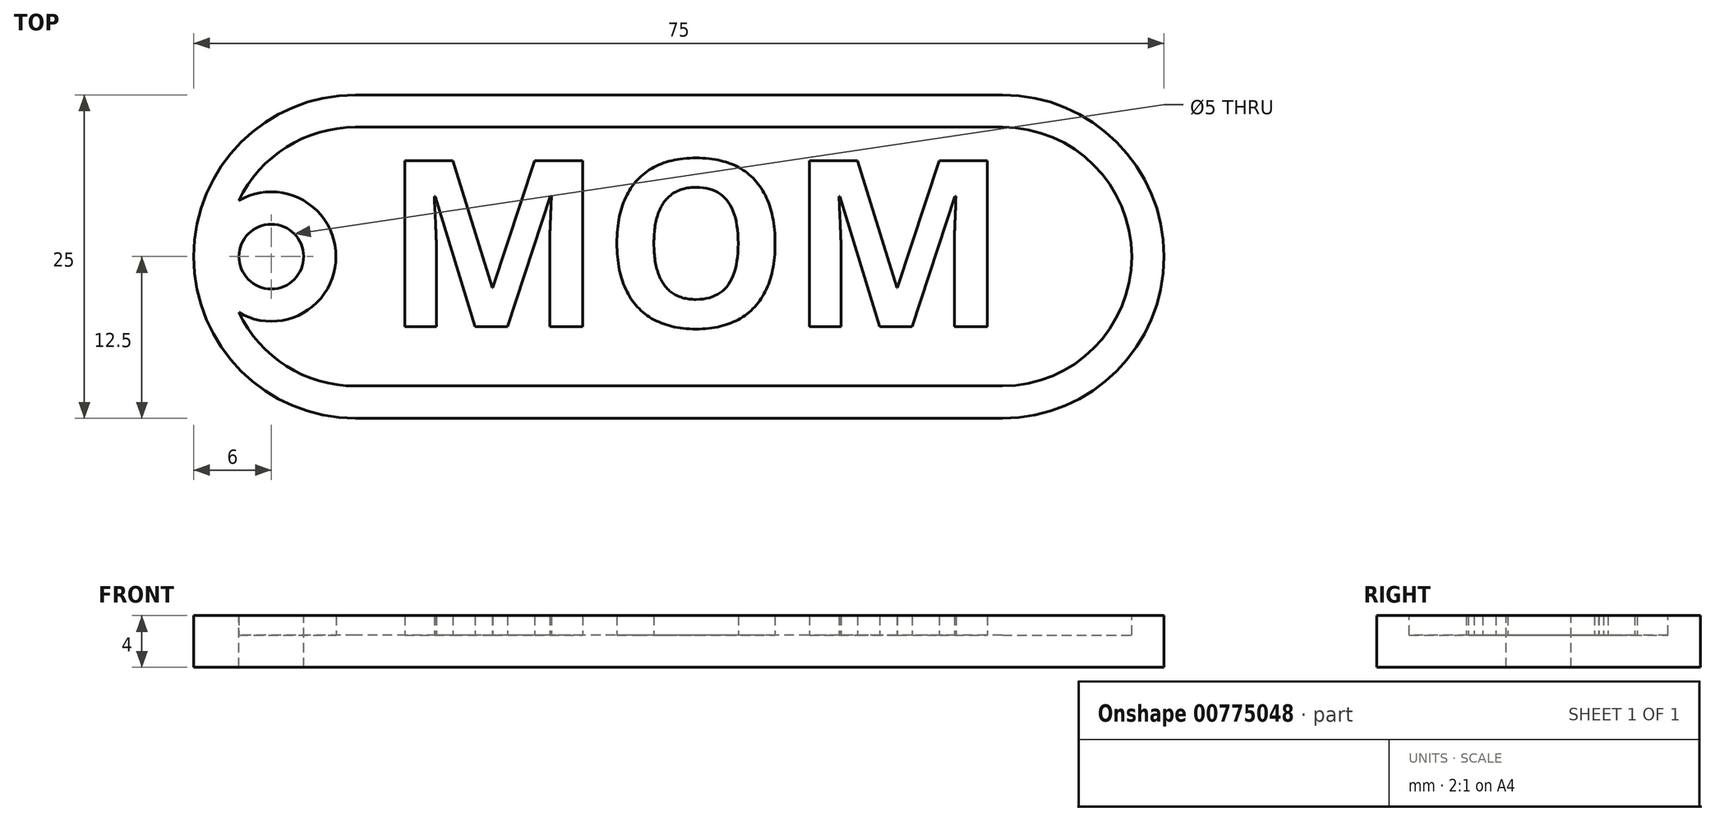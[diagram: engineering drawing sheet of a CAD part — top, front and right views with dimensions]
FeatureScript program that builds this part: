
annotation { "Feature Type Name" : "Feature", "Feature Type Description" : "" }
export const myFeature = defineFeature(function(context is Context, id is Id, definition is map)
    precondition{}
    {
        {
            var Q0;
            Q0=qCreatedBy(makeId("Top.planeOp"),FACE);
            var sketch = newSketch(context, id + "F0", { "sketchPlane" : qUnion([Q0])});
            skLineSegment(sketch, "E0.bottom", {"start": v(0, 0) * mm, "end": v(62.5, 0) * mm});
            skLineSegment(sketch, "E0.top", {"start": v(12.5, 25) * mm, "end": v(62.5, 25) * mm});
            skArc(sketch, "E1", {"start": v(12.5, 25) * mm, "mid": v(0, 12.5) * mm, "end": v(12.5, 0) * mm});
            skPoint(sketch, "E1.centerSnap0", {"position": v(0, 12.5) * mm});
            skArc(sketch, "E2", {"start": v(62.5, 0) * mm, "mid": v(75, 12.5) * mm, "end": v(62.5, 25) * mm});
            skPoint(sketch, "E2.centerSnap0", {"position": v(75, 12.5) * mm});
            skPoint(sketch, "E3.orphan", {"position": v(0, 25) * mm});
            skPoint(sketch, "E4.orphan", {"position": v(75, 25) * mm});
            skPoint(sketch, "E5.orphan", {"position": v(75, 0) * mm});
            skSolve(sketch);
        }
        {
            var Q0;
            Q0=makeQuery(id+"F0.imprint","IMPRINT",FACE,{"disambiguationData":[TD([[makeQuery(id+"F0.imprint","IMPRINT",EDGE,{"derivedFrom":sQuery(id+"F0.wireOp",EDGE,"E0.top")}),-1.0]])]});
            extrude(context, id + "F1", {"entities" : qUnion([Q0]), "depth" : 4 * mm, "offsetDistance" : 25 * mm});
        }
        {
            var Q0;
            Q0=makeQuery(id+"F1.opExtrude","CAP_FACE",FACE,{"disambiguationData":[OSD([sQuery(id+"F0.wireOp",EDGE,"E0.bottom"),sQuery(id+"F0.wireOp",EDGE,"E0.top"),sQuery(id+"F0.wireOp",EDGE,"E1"),sQuery(id+"F0.wireOp",EDGE,"E2")])],"isStart":false});
            var sketch = newSketch(context, id + "F2", { "sketchPlane" : qUnion([Q0])});
            skArc(sketch, "E6", {"start": v(12.5, 22.5) * mm, "mid": v(2.5, 12.5) * mm, "end": v(12.5, 2.5) * mm});
            skArc(sketch, "E7", {"start": v(62.5, 2.5) * mm, "mid": v(72.5, 12.5) * mm, "end": v(62.5, 22.5) * mm});
            skLineSegment(sketch, "E8", {"start": v(12.5, 22.5) * mm, "end": v(62.5, 22.5) * mm});
            skLineSegment(sketch, "E9", {"start": v(62.5, 2.5) * mm, "end": v(12.5, 2.5) * mm});
            skSolve(sketch);
        }
        {
            var Q0;
            Q0=makeQuery(id+"F2.imprint","IMPRINT",FACE,{"disambiguationData":[TD([[makeQuery(id+"F2.imprint","IMPRINT",EDGE,{"derivedFrom":sQuery(id+"F2.wireOp",EDGE,"E6")}),1.0]])]});
            extrude(context, id + "F3", {"entities" : qUnion([Q0]), "operationType" : NewBodyOperationType.REMOVE, "oppositeDirection" : true, "depth" : 1.5 * mm, "offsetDistance" : 25 * mm});
        }
        {
            var Q0;
            Q0=makeQuery(id+"F3.boolean.opBoolean","COPY",FACE,{"derivedFrom":makeQuery(id+"F3.opExtrude","CAP_FACE",FACE,{"disambiguationData":[OSD([sQuery(id+"F2.wireOp",EDGE,"E6"),sQuery(id+"F2.wireOp",EDGE,"E7"),sQuery(id+"F2.wireOp",EDGE,"E8"),sQuery(id+"F2.wireOp",EDGE,"E9")])],"isStart":false})});
            var sketch = newSketch(context, id + "F4", { "sketchPlane" : qUnion([Q0])});
            skCircle(sketch, "E10", {"center": v(6, 12.5) * mm, "radius": 5 * mm});
            skPoint(sketch, "E10.centerSnap0", {"position": v(2.5, 12.5) * mm});
            skSolve(sketch);
        }
        {
            var Q0;
            {var subQ0=sQuery(id+"F4.wireOp",EDGE,"E10");var subQ1=makeQuery(id+"F3.boolean.opBoolean","COPY",EDGE,{"derivedFrom":makeQuery(id+"F3.opExtrude","CAP_EDGE",EDGE,{"disambiguationData":[OSD([sQuery(id+"F2.wireOp",EDGE,"E6")])],"isStart":false})});var subQ2=makeQuery(id+"F4.imprint","INTERSECT",VERTEX,{"disambiguationData":[OD(0.0)],"derivedFrom":[subQ1,subQ0]});Q0=makeQuery(id+"F4.imprint","IMPRINT",FACE,{"disambiguationData":[TD([[makeQuery(id+"F4.imprint","IMPRINT",EDGE,{"disambiguationData":[TD([[subQ2,1.0]])],"derivedFrom":subQ0}),1.0]])]});}
            extrude(context, id + "F5", {"entities" : qUnion([Q0]), "operationType" : NewBodyOperationType.ADD, "depth" : 1.5 * mm, "offsetDistance" : 25 * mm});
        }
        {
            var Q0;
            Q0=makeQuery(id+"F5.boolean.opBoolean","MERGE",FACE,{"derivedFrom":[makeQuery(id+"F1.opExtrude","CAP_FACE",FACE,{"disambiguationData":[OSD([sQuery(id+"F0.wireOp",EDGE,"E0.bottom"),sQuery(id+"F0.wireOp",EDGE,"E0.top"),sQuery(id+"F0.wireOp",EDGE,"E1"),sQuery(id+"F0.wireOp",EDGE,"E2")])],"isStart":false}),makeQuery(id+"F5.opExtrude","CAP_FACE",FACE,{"disambiguationData":[OSD([sQuery(id+"F2.wireOp",EDGE,"E6"),sQuery(id+"F4.wireOp",EDGE,"E10")])],"isStart":false})]});
            var sketch = newSketch(context, id + "F6", { "sketchPlane" : qUnion([Q0])});
            skCircle(sketch, "E11", {"center": v(6, 12.5) * mm, "radius": 2.5 * mm});
            skSolve(sketch);
        }
        {
            var Q0;
            Q0=makeQuery(id+"F6.imprint","IMPRINT",FACE,{"disambiguationData":[TD([[makeQuery(id+"F6.imprint","IMPRINT",EDGE,{"derivedFrom":sQuery(id+"F6.wireOp",EDGE,"E11")}),1.0]])]});
            extrude(context, id + "F7", {"entities" : qUnion([Q0]), "operationType" : NewBodyOperationType.REMOVE, "oppositeDirection" : true, "depth" : 25 * mm, "offsetDistance" : 25 * mm});
        }
        {
            var Q0;
            Q0=makeQuery(id+"F3.boolean.opBoolean","COPY",FACE,{"derivedFrom":makeQuery(id+"F3.opExtrude","CAP_FACE",FACE,{"disambiguationData":[OSD([sQuery(id+"F2.wireOp",EDGE,"E6"),sQuery(id+"F2.wireOp",EDGE,"E7"),sQuery(id+"F2.wireOp",EDGE,"E8"),sQuery(id+"F2.wireOp",EDGE,"E9")])],"isStart":false})});
            var sketch = newSketch(context, id + "F8", { "sketchPlane" : qUnion([Q0])});
            skText(sketch, "E12", { "text": "MOM", "fontName": "OpenSans-Bold.ttf"});
            const initialGuessF8  = {"E12": [0.01471, 0.00708, 1, 0, 0.01295]};
            skSetInitialGuess(sketch, initialGuessF8);
            skSolve(sketch);
        }
        {
            var Q0;
            Q0 = qSketchRegion(id + "F8", true);
            extrude(context, id + "F9", {"entities" : qUnion([Q0]), "operationType" : NewBodyOperationType.ADD, "depth" : 1.5 * mm, "offsetDistance" : 25 * mm});
        }
    });
